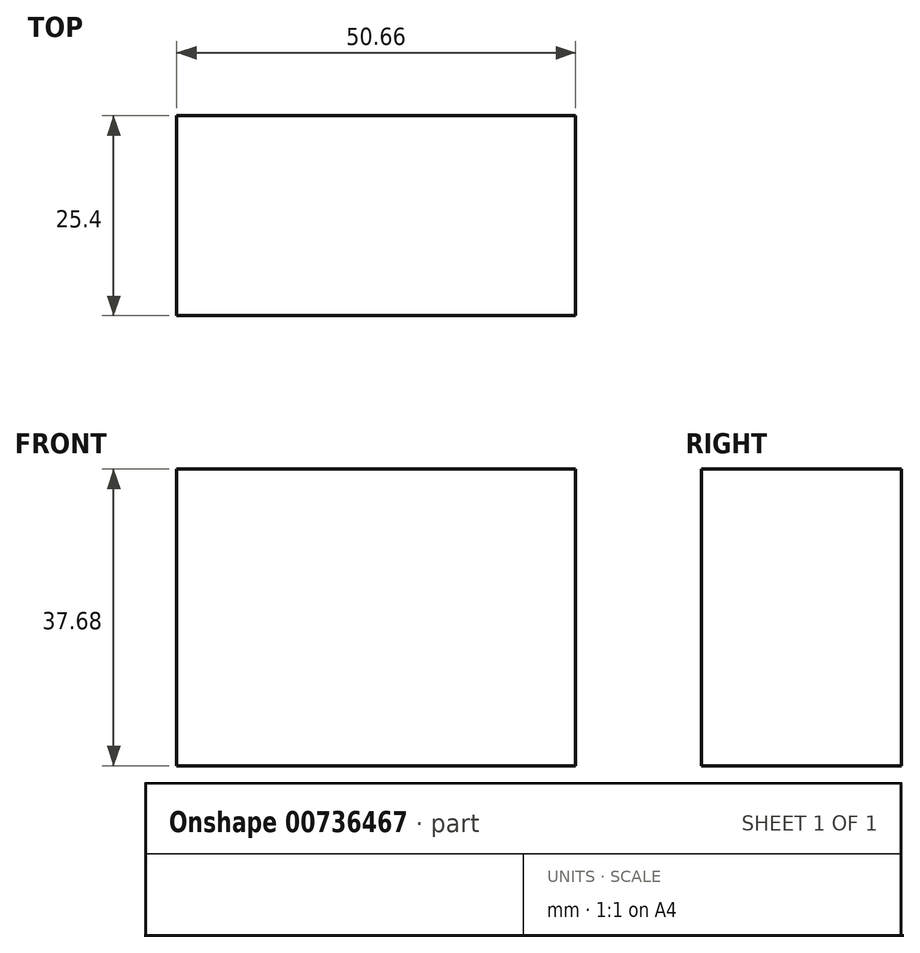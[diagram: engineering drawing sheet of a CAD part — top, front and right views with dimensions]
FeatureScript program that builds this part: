
annotation { "Feature Type Name" : "Feature", "Feature Type Description" : "" }
export const myFeature = defineFeature(function(context is Context, id is Id, definition is map)
    precondition{}
    {
        {
            var Q0;
            Q0=qCreatedBy(makeId("Front.planeOp"),FACE);
            var sketch = newSketch(context, id + "F0", { "sketchPlane" : qUnion([Q0])});
            skLineSegment(sketch, "E0.bottom", {"start": v(0, 0) * mm, "end": v(50.66, 0) * mm});
            skLineSegment(sketch, "E0.top", {"start": v(0, 37.68) * mm, "end": v(50.66, 37.68) * mm});
            skLineSegment(sketch, "E0.left", {"start": v(0, 0) * mm, "end": v(0, 37.68) * mm});
            skLineSegment(sketch, "E0.right", {"start": v(50.66, 0) * mm, "end": v(50.66, 37.68) * mm});
            skSolve(sketch);
        }
        {
            var Q0;
            Q0=makeQuery(id+"F0.imprint","IMPRINT",FACE,{"disambiguationData":[TD([[makeQuery(id+"F0.imprint","IMPRINT",EDGE,{"derivedFrom":sQuery(id+"F0.wireOp",EDGE,"E0.bottom")}),1.0]])]});
            extrude(context, id + "F1", {"entities" : qUnion([Q0]), "depth" : 25.4 * mm, "offsetDistance" : 25.4 * mm});
        }
    });
